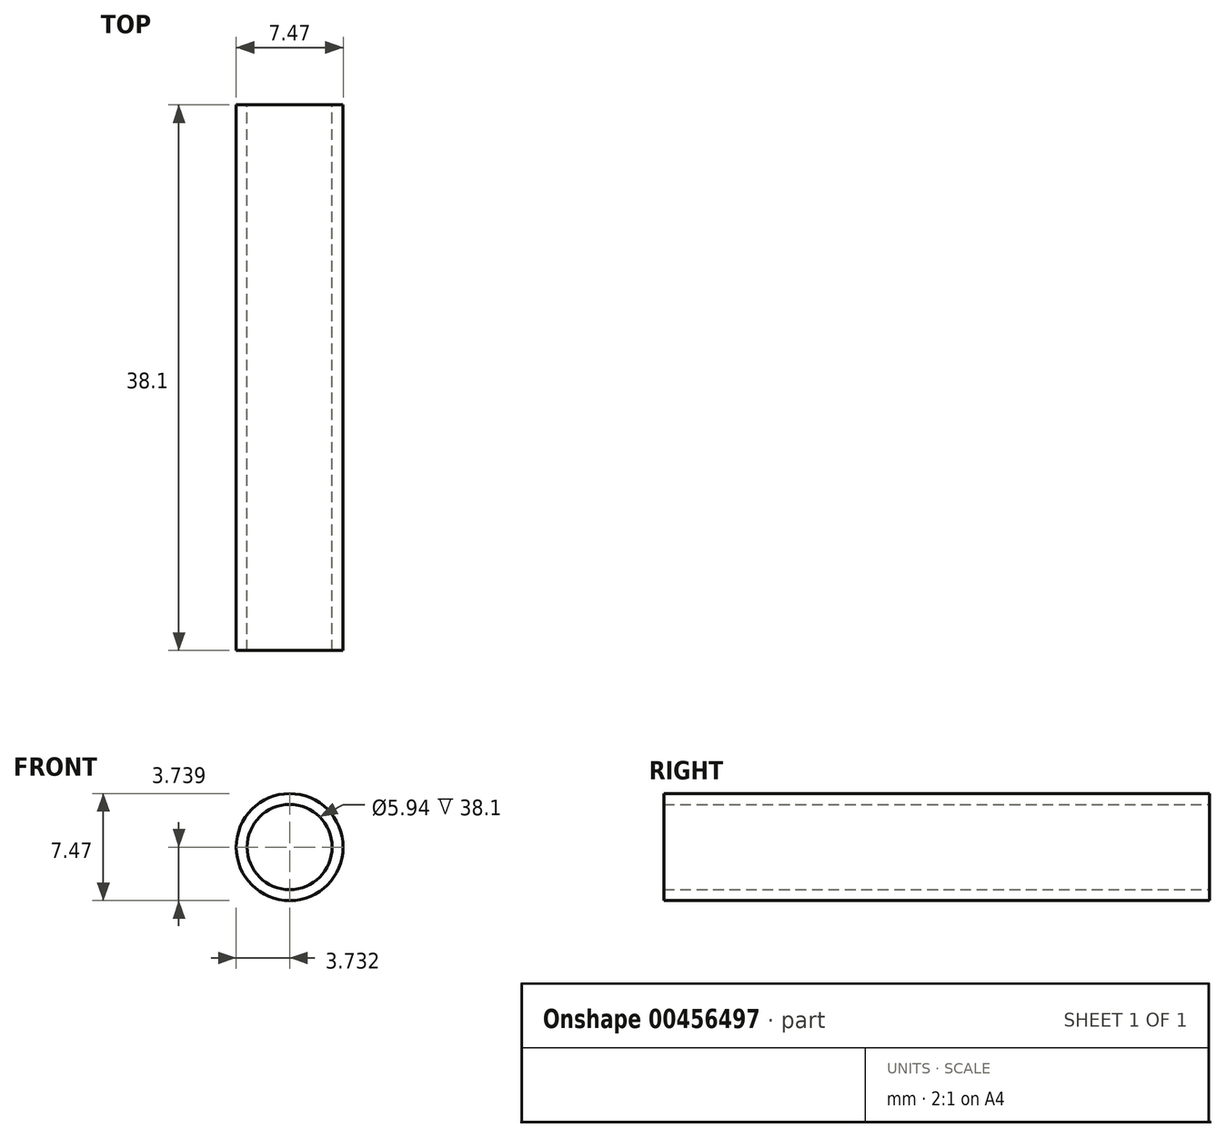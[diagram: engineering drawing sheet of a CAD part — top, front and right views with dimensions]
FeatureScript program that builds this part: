
annotation { "Feature Type Name" : "Feature", "Feature Type Description" : "" }
export const myFeature = defineFeature(function(context is Context, id is Id, definition is map)
    precondition{}
    {
        {
            var Q0;
            Q0=qCreatedBy(makeId("Front.planeOp"),FACE);
            var sketch = newSketch(context, id + "F0", { "sketchPlane" : qUnion([Q0])});
            skCircle(sketch, "E0", {"center": v(-46.92, 21.1) * mm, "radius": 2.97 * mm});
            skCircle(sketch, "E1", {"center": v(-46.92, 21.1) * mm, "radius": 3.73 * mm});
            skSolve(sketch);
        }
        {
            var Q0;
            Q0 = qSketchRegion(id + "F0", true);
            extrude(context, id + "F1", {"entities" : qUnion([Q0]), "depth" : 38.1 * mm, "offsetDistance" : 25.4 * mm});
        }
    });
